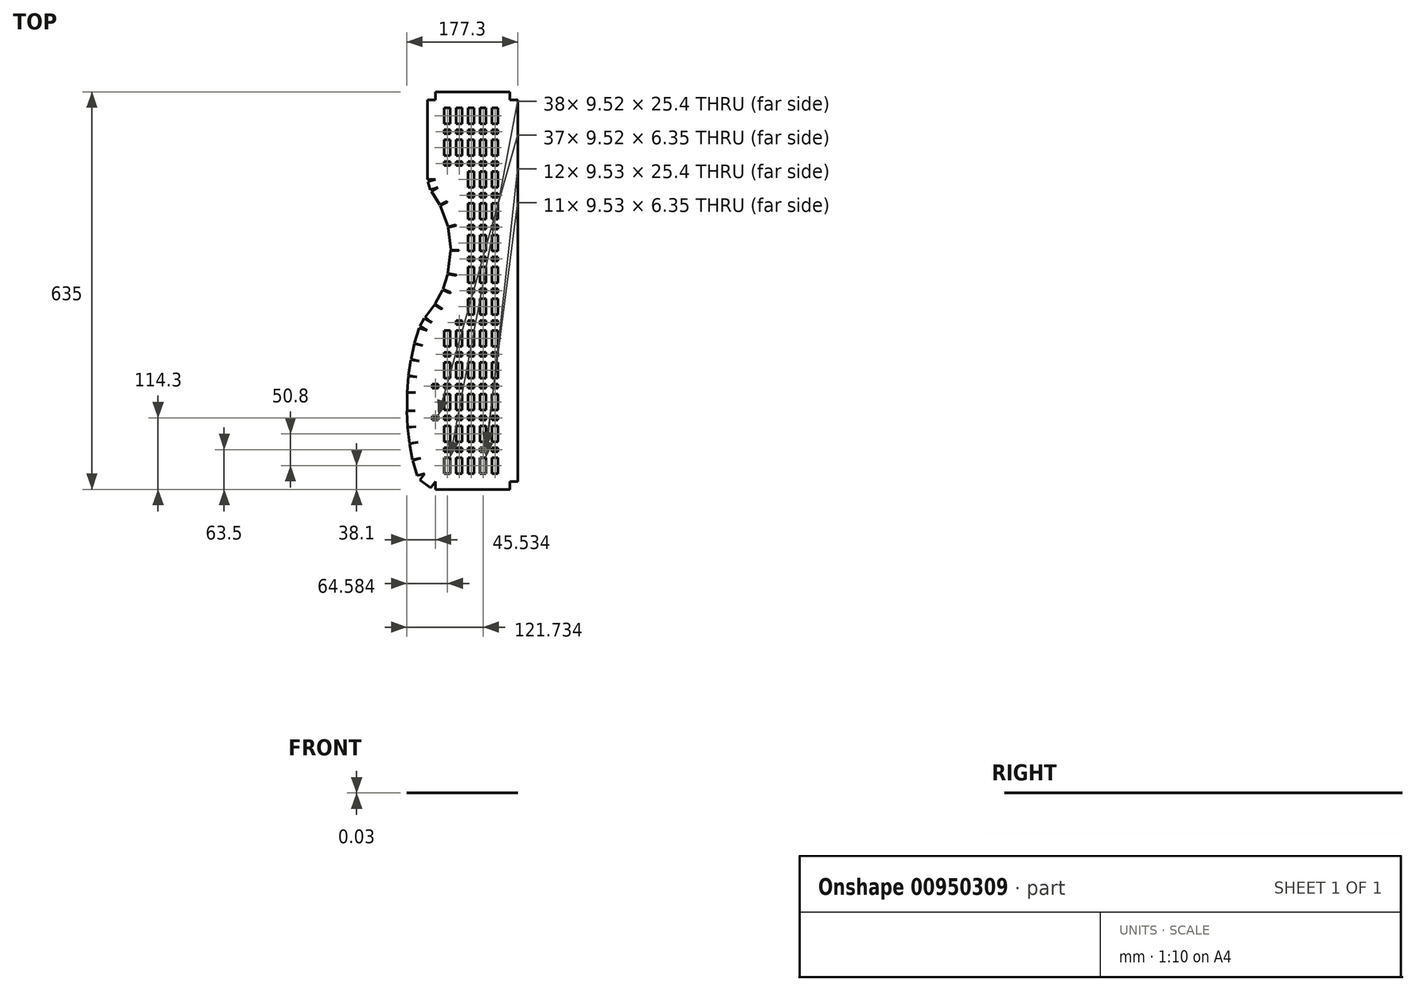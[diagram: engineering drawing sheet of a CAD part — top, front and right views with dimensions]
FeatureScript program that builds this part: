
annotation { "Feature Type Name" : "Feature", "Feature Type Description" : "" }
export const myFeature = defineFeature(function(context is Context, id is Id, definition is map)
    precondition{}
    {
        {
            var Q0;
            Q0=qCreatedBy(makeId("Top.planeOp"),FACE);
            var sketch = newSketch(context, id + "F0", { "sketchPlane" : qUnion([Q0])});
            skLineSegment(sketch, "E0", {"start": v(0, 0) * mm, "end": v(118.85, 0) * mm, "construction": true});
            skLineSegment(sketch, "E1", {"start": v(118.85, 0) * mm, "end": v(118.85, -609.6) * mm, "construction": true});
            skLineSegment(sketch, "E2", {"start": v(118.85, -609.6) * mm, "end": v(0, -609.6) * mm, "construction": true});
            skLineSegment(sketch, "E3", {"start": v(0, -622.3) * mm, "end": v(118.85, -622.3) * mm});
            skLineSegment(sketch, "E4", {"start": v(118.85, -622.3) * mm, "end": v(118.85, -609.6) * mm});
            skLineSegment(sketch, "E5", {"start": v(118.85, -609.6) * mm, "end": v(131.55, -609.6) * mm});
            skLineSegment(sketch, "E6", {"start": v(131.55, -609.6) * mm, "end": v(131.55, 0) * mm});
            skLineSegment(sketch, "E7", {"start": v(131.55, 0) * mm, "end": v(118.85, 0) * mm});
            skLineSegment(sketch, "E8", {"start": v(118.85, 0) * mm, "end": v(118.85, 12.7) * mm});
            skLineSegment(sketch, "E9", {"start": v(118.85, 12.7) * mm, "end": v(0, 12.7) * mm});
            skLineSegment(sketch, "E10", {"start": v(0, 12.7) * mm, "end": v(0, 0) * mm});
            skArc(sketch, "E11", {"start": v(0, -609.6) * mm, "mid": v(-10.58, -606.07) * mm, "end": v(-16.91, -596.9) * mm, "construction": true});
            skArc(sketch, "E12", {"start": v(-16.91, -596.9) * mm, "mid": v(-32.27, -482.32) * mm, "end": v(-13.22, -368.3) * mm, "construction": true});
            skLineSegment(sketch, "E13", {"start": v(-16.91, -596.9) * mm, "end": v(-13.22, -609.6) * mm, "construction": true});
            skPoint(sketch, "E14", {"position": v(-32.27, -482.32) * mm});
            skArc(sketch, "E15", {"start": v(-13.22, -368.3) * mm, "mid": v(-10.23, -361.57) * mm, "end": v(-5.93, -355.6) * mm, "construction": true});
            skArc(sketch, "E16", {"start": v(-5.93, -355.6) * mm, "mid": v(37.39, -249.44) * mm, "end": v(4.17, -139.7) * mm, "construction": true});
            skArc(sketch, "E17", {"start": v(4.17, -139.7) * mm, "mid": v(1.07, -133.68) * mm, "end": v(0, -127) * mm, "construction": true});
            skLineSegment(sketch, "E18", {"start": v(0, -127) * mm, "end": v(0, 0) * mm, "construction": true});
            skLineSegment(sketch, "E19", {"start": v(0, -609.6) * mm, "end": v(-7.63, -619.76) * mm});
            skLineSegment(sketch, "E20", {"start": v(-7.63, -619.76) * mm, "end": v(-24.54, -607.06) * mm});
            skLineSegment(sketch, "E21", {"start": v(-24.54, -607.06) * mm, "end": v(-16.91, -596.9) * mm});
            skLineSegment(sketch, "E22", {"start": v(0, -609.6) * mm, "end": v(0, -622.3) * mm});
            skLineSegment(sketch, "E23", {"start": v(-19.03, -599.72) * mm, "end": v(-2.12, -612.42) * mm, "construction": true});
            skPoint(sketch, "E24", {"position": v(-10.58, -606.07) * mm});
            skLineSegment(sketch, "E25", {"start": v(-10.58, -606.07) * mm, "end": v(-16.08, -613.4) * mm, "construction": true});
            skLineSegment(sketch, "E26", {"start": v(-16.91, -596.9) * mm, "end": v(-29.1, -600.44) * mm});
            skLineSegment(sketch, "E27", {"start": v(-29.1, -600.44) * mm, "end": v(-36.2, -576.05) * mm});
            skLineSegment(sketch, "E28", {"start": v(-36.2, -576.05) * mm, "end": v(-23.2, -572.28) * mm});
            skLineSegment(sketch, "E29", {"start": v(-23.2, -572.28) * mm, "end": v(-36.5, -574.76) * mm});
            skLineSegment(sketch, "E30", {"start": v(-36.5, -574.76) * mm, "end": v(-41.16, -549.79) * mm});
            skLineSegment(sketch, "E31", {"start": v(-41.16, -549.79) * mm, "end": v(-27.86, -547.3) * mm});
            skLineSegment(sketch, "E32", {"start": v(-27.86, -547.3) * mm, "end": v(-41.3, -548.91) * mm});
            skLineSegment(sketch, "E33", {"start": v(-41.3, -548.91) * mm, "end": v(-44.31, -523.7) * mm});
            skLineSegment(sketch, "E34", {"start": v(-44.31, -523.7) * mm, "end": v(-30.88, -522.09) * mm});
            skLineSegment(sketch, "E35", {"start": v(-30.88, -522.09) * mm, "end": v(-44.39, -522.81) * mm});
            skLineSegment(sketch, "E36", {"start": v(-44.39, -522.81) * mm, "end": v(-45.75, -497.45) * mm});
            skLineSegment(sketch, "E37", {"start": v(-45.75, -497.45) * mm, "end": v(-32.24, -496.72) * mm});
            skLineSegment(sketch, "E38", {"start": v(-32.24, -496.72) * mm, "end": v(-45.3, -496.72) * mm});
            skLineSegment(sketch, "E39", {"start": v(-45.3, -496.72) * mm, "end": v(-45.3, -467.92) * mm});
            skLineSegment(sketch, "E40", {"start": v(-45.3, -467.92) * mm, "end": v(-31.78, -467.92) * mm});
            skLineSegment(sketch, "E41", {"start": v(-32.27, -482.32) * mm, "end": v(-45.3, -482.32) * mm, "construction": true});
            skLineSegment(sketch, "E42", {"start": v(-31.78, -467.92) * mm, "end": v(-45.26, -466.76) * mm});
            skLineSegment(sketch, "E43", {"start": v(-45.26, -466.76) * mm, "end": v(-43.08, -441.45) * mm});
            skLineSegment(sketch, "E44", {"start": v(-43.08, -441.45) * mm, "end": v(-29.6, -442.61) * mm});
            skLineSegment(sketch, "E45", {"start": v(-33.51, -389.79) * mm, "end": v(-20.3, -392.7) * mm});
            skLineSegment(sketch, "E46", {"start": v(-20.3, -392.7) * mm, "end": v(-33.3, -388.93) * mm});
            skLineSegment(sketch, "E47", {"start": v(-33.3, -388.93) * mm, "end": v(-26.22, -364.53) * mm});
            skLineSegment(sketch, "E48", {"start": v(-26.22, -364.53) * mm, "end": v(-13.22, -368.3) * mm});
            skLineSegment(sketch, "E49", {"start": v(-38.98, -414.6) * mm, "end": v(-33.51, -389.79) * mm});
            skLineSegment(sketch, "E50", {"start": v(-38.98, -414.6) * mm, "end": v(-25.76, -417.5) * mm});
            skLineSegment(sketch, "E51", {"start": v(-25.76, -417.5) * mm, "end": v(-39.14, -415.46) * mm});
            skLineSegment(sketch, "E52", {"start": v(-39.14, -415.46) * mm, "end": v(-42.97, -440.57) * mm});
            skLineSegment(sketch, "E53", {"start": v(-42.97, -440.57) * mm, "end": v(-29.6, -442.61) * mm});
            skLineSegment(sketch, "E54", {"start": v(-23.2, -572.28) * mm, "end": v(-27.86, -547.3) * mm, "construction": true});
            skLineSegment(sketch, "E55", {"start": v(-27.86, -547.3) * mm, "end": v(-30.88, -522.09) * mm, "construction": true});
            skLineSegment(sketch, "E56", {"start": v(-30.88, -522.09) * mm, "end": v(-32.24, -496.72) * mm, "construction": true});
            skLineSegment(sketch, "E57", {"start": v(-31.78, -467.92) * mm, "end": v(-29.6, -442.61) * mm, "construction": true});
            skLineSegment(sketch, "E58", {"start": v(-29.6, -442.61) * mm, "end": v(-25.76, -417.5) * mm, "construction": true});
            skLineSegment(sketch, "E59", {"start": v(-25.76, -417.5) * mm, "end": v(-20.3, -392.7) * mm, "construction": true});
            skLineSegment(sketch, "E60", {"start": v(-20.3, -392.7) * mm, "end": v(-13.22, -368.3) * mm, "construction": true});
            skLineSegment(sketch, "E61", {"start": v(-13.22, -368.3) * mm, "end": v(-5.93, -355.6) * mm, "construction": true});
            skLineSegment(sketch, "E62", {"start": v(-5.93, -355.6) * mm, "end": v(-17.66, -348.86) * mm});
            skLineSegment(sketch, "E63", {"start": v(-17.66, -348.86) * mm, "end": v(-24.96, -361.56) * mm});
            skLineSegment(sketch, "E64", {"start": v(-24.96, -361.56) * mm, "end": v(-13.22, -368.3) * mm});
            skLineSegment(sketch, "E65", {"start": v(-5.93, -355.6) * mm, "end": v(-16.67, -347.37) * mm});
            skLineSegment(sketch, "E66", {"start": v(-16.67, -347.37) * mm, "end": v(-1.22, -327.2) * mm});
            skLineSegment(sketch, "E67", {"start": v(-1.22, -327.2) * mm, "end": v(9.52, -335.44) * mm, "construction": true});
            skLineSegment(sketch, "E68", {"start": v(9.52, -335.44) * mm, "end": v(-5.93, -355.6) * mm, "construction": true});
            skLineSegment(sketch, "E69", {"start": v(-0.53, -326.14) * mm, "end": v(11.44, -332.45) * mm, "construction": true});
            skLineSegment(sketch, "E70", {"start": v(11.44, -332.45) * mm, "end": v(23.28, -309.98) * mm, "construction": true});
            skLineSegment(sketch, "E71", {"start": v(23.28, -309.98) * mm, "end": v(11.31, -303.67) * mm, "construction": true});
            skLineSegment(sketch, "E72", {"start": v(11.31, -303.67) * mm, "end": v(-0.53, -326.14) * mm});
            skLineSegment(sketch, "E73", {"start": v(-0.53, -326.14) * mm, "end": v(10.83, -333.41) * mm});
            skLineSegment(sketch, "E74", {"start": v(-1.22, -327.2) * mm, "end": v(10.15, -334.48) * mm});
            skCircle(sketch, "E75", {"center": v(-0.53, -326.14) * mm, "radius": 1.27 * mm, "construction": true});
            skLineSegment(sketch, "E76", {"start": v(10.15, -334.48) * mm, "end": v(9.52, -335.44) * mm, "construction": true});
            skLineSegment(sketch, "E77", {"start": v(10.83, -333.41) * mm, "end": v(11.44, -332.45) * mm, "construction": true});
            skArc(sketch, "E78", {"start": v(10.15, -334.48) * mm, "mid": v(10.49, -333.95) * mm, "end": v(10.83, -333.41) * mm});
            skLineSegment(sketch, "E79", {"start": v(11.31, -303.67) * mm, "end": v(23.74, -308.93) * mm});
            skLineSegment(sketch, "E80", {"start": v(23.28, -309.98) * mm, "end": v(23.74, -308.93) * mm, "construction": true});
            skLineSegment(sketch, "E81", {"start": v(24.67, -306.7) * mm, "end": v(11.8, -302.5) * mm, "construction": true});
            skLineSegment(sketch, "E82", {"start": v(11.8, -302.5) * mm, "end": v(24.23, -307.76) * mm});
            skLineSegment(sketch, "E83", {"start": v(24.67, -306.7) * mm, "end": v(32.57, -282.57) * mm, "construction": true});
            skLineSegment(sketch, "E84", {"start": v(32.57, -282.57) * mm, "end": v(19.7, -278.36) * mm, "construction": true});
            skLineSegment(sketch, "E85", {"start": v(19.7, -278.36) * mm, "end": v(11.8, -302.5) * mm});
            skCircle(sketch, "E86", {"center": v(11.8, -302.5) * mm, "radius": 1.27 * mm, "construction": true});
            skLineSegment(sketch, "E87", {"start": v(24.67, -306.7) * mm, "end": v(24.23, -307.76) * mm, "construction": true});
            skArc(sketch, "E88", {"start": v(23.74, -308.93) * mm, "mid": v(23.99, -308.35) * mm, "end": v(24.23, -307.76) * mm});
            skLineSegment(sketch, "E89", {"start": v(19.7, -278.36) * mm, "end": v(32.9, -281.23) * mm});
            skLineSegment(sketch, "E90", {"start": v(37.57, -241.14) * mm, "end": v(24.13, -241.15) * mm});
            skLineSegment(sketch, "E91", {"start": v(24.13, -241.15) * mm, "end": v(37.57, -242.67) * mm, "construction": true});
            skLineSegment(sketch, "E92", {"start": v(20.04, -277.13) * mm, "end": v(33.18, -280) * mm});
            skLineSegment(sketch, "E93", {"start": v(20.04, -277.13) * mm, "end": v(33.49, -278.66) * mm, "construction": true});
            skLineSegment(sketch, "E94", {"start": v(33.49, -278.66) * mm, "end": v(37.57, -242.67) * mm, "construction": true});
            skLineSegment(sketch, "E95", {"start": v(24.13, -241.15) * mm, "end": v(20.04, -277.13) * mm});
            skCircle(sketch, "E96", {"center": v(20.04, -277.13) * mm, "radius": 1.27 * mm, "construction": true});
            skLineSegment(sketch, "E97", {"start": v(33.18, -280) * mm, "end": v(33.49, -278.66) * mm, "construction": true});
            skLineSegment(sketch, "E98", {"start": v(32.9, -281.23) * mm, "end": v(32.57, -282.57) * mm, "construction": true});
            skPoint(sketch, "E99", {"position": v(37.58, -241.42) * mm});
            skCircle(sketch, "E100", {"center": v(24.13, -241.15) * mm, "radius": 1.27 * mm, "construction": true});
            skLineSegment(sketch, "E101", {"start": v(37.57, -241.14) * mm, "end": v(37.57, -242.67) * mm, "construction": true});
            skArc(sketch, "E102", {"start": v(33.18, -280) * mm, "mid": v(33.04, -280.62) * mm, "end": v(32.9, -281.23) * mm});
            skLineSegment(sketch, "E103", {"start": v(0, 0) * mm, "end": v(-12.7, 0) * mm});
            skLineSegment(sketch, "E104", {"start": v(-12.7, 0) * mm, "end": v(-12.7, -127) * mm});
            skLineSegment(sketch, "E105", {"start": v(-12.7, -127) * mm, "end": v(0, -127) * mm});
            skLineSegment(sketch, "E106", {"start": v(0, -127) * mm, "end": v(4.17, -139.7) * mm, "construction": true});
            skLineSegment(sketch, "E107", {"start": v(4.17, -139.7) * mm, "end": v(-7.9, -143.66) * mm});
            skLineSegment(sketch, "E108", {"start": v(-7.9, -143.66) * mm, "end": v(-12.07, -130.96) * mm});
            skLineSegment(sketch, "E109", {"start": v(-12.07, -130.96) * mm, "end": v(0, -127) * mm});
            skLineSegment(sketch, "E110", {"start": v(4.17, -139.7) * mm, "end": v(-6.59, -146.45) * mm});
            skLineSegment(sketch, "E111", {"start": v(-6.59, -146.45) * mm, "end": v(6.92, -167.96) * mm});
            skLineSegment(sketch, "E112", {"start": v(6.92, -167.96) * mm, "end": v(17.67, -161.21) * mm, "construction": true});
            skLineSegment(sketch, "E113", {"start": v(17.67, -161.21) * mm, "end": v(4.17, -139.7) * mm, "construction": true});
            skLineSegment(sketch, "E114", {"start": v(6.92, -167.96) * mm, "end": v(18.27, -162.35) * mm});
            skLineSegment(sketch, "E115", {"start": v(18.27, -162.35) * mm, "end": v(17.67, -161.21) * mm, "construction": true});
            skLineSegment(sketch, "E116", {"start": v(7.53, -169.08) * mm, "end": v(18.85, -163.48) * mm});
            skLineSegment(sketch, "E117", {"start": v(18.85, -163.48) * mm, "end": v(19.43, -164.62) * mm, "construction": true});
            skLineSegment(sketch, "E118", {"start": v(19.43, -164.62) * mm, "end": v(7.53, -169.08) * mm, "construction": true});
            skLineSegment(sketch, "E119", {"start": v(7.53, -169.08) * mm, "end": v(20.24, -203) * mm});
            skLineSegment(sketch, "E120", {"start": v(20.24, -203) * mm, "end": v(32.13, -198.54) * mm, "construction": true});
            skLineSegment(sketch, "E121", {"start": v(32.13, -198.54) * mm, "end": v(19.43, -164.62) * mm, "construction": true});
            skCircle(sketch, "E122", {"center": v(6.92, -167.96) * mm, "radius": 1.27 * mm, "construction": true});
            skLineSegment(sketch, "E123", {"start": v(20.24, -203) * mm, "end": v(32.5, -200) * mm});
            skLineSegment(sketch, "E124", {"start": v(32.5, -200) * mm, "end": v(32.13, -198.54) * mm, "construction": true});
            skLineSegment(sketch, "E125", {"start": v(32.8, -201.22) * mm, "end": v(20.54, -204.23) * mm});
            skLineSegment(sketch, "E126", {"start": v(20.54, -204.23) * mm, "end": v(33.14, -202.68) * mm, "construction": true});
            skLineSegment(sketch, "E127", {"start": v(32.8, -201.22) * mm, "end": v(33.14, -202.68) * mm, "construction": true});
            skCircle(sketch, "E128", {"center": v(20.54, -204.23) * mm, "radius": 1.27 * mm, "construction": true});
            skLineSegment(sketch, "E129", {"start": v(24.95, -240.18) * mm, "end": v(37.57, -240.17) * mm});
            skLineSegment(sketch, "E130", {"start": v(20.54, -204.23) * mm, "end": v(24.95, -240.18) * mm});
            skLineSegment(sketch, "E131", {"start": v(24.95, -240.18) * mm, "end": v(37.55, -238.63) * mm, "construction": true});
            skLineSegment(sketch, "E132", {"start": v(37.55, -238.63) * mm, "end": v(37.57, -240.17) * mm, "construction": true});
            skLineSegment(sketch, "E133", {"start": v(37.55, -238.63) * mm, "end": v(33.14, -202.68) * mm, "construction": true});
            skArc(sketch, "E134", {"start": v(37.57, -241.14) * mm, "mid": v(37.57, -240.65) * mm, "end": v(37.57, -240.17) * mm});
            skArc(sketch, "E135", {"start": v(32.8, -201.22) * mm, "mid": v(32.65, -200.6) * mm, "end": v(32.5, -200) * mm});
            skArc(sketch, "E136", {"start": v(18.85, -163.48) * mm, "mid": v(18.56, -162.91) * mm, "end": v(18.27, -162.35) * mm});
            skLineSegment(sketch, "E137.0", {"start": v(12.7, -127) * mm, "end": v(12.7, -12.7) * mm, "construction": true});
            skArc(sketch, "E137.1", {"start": v(14.4, -132.17) * mm, "mid": v(13.14, -129.72) * mm, "end": v(12.7, -127) * mm, "construction": true});
            skLineSegment(sketch, "E137.2", {"start": v(12.7, -12.7) * mm, "end": v(106.15, -12.7) * mm, "construction": true});
            skArc(sketch, "E137.3", {"start": v(3.55, -364.05) * mm, "mid": v(50.07, -250.03) * mm, "end": v(14.4, -132.17) * mm, "construction": true});
            skArc(sketch, "E137.4", {"start": v(-1.15, -372.23) * mm, "mid": v(0.78, -367.9) * mm, "end": v(3.55, -364.05) * mm, "construction": true});
            skLineSegment(sketch, "E137.5", {"start": v(106.15, -12.7) * mm, "end": v(106.15, -596.9) * mm, "construction": true});
            skLineSegment(sketch, "E137.6", {"start": v(106.15, -596.9) * mm, "end": v(0, -596.9) * mm, "construction": true});
            skArc(sketch, "E137.7", {"start": v(0, -596.9) * mm, "mid": v(-2.95, -595.92) * mm, "end": v(-4.72, -593.36) * mm, "construction": true});
            skArc(sketch, "E137.8", {"start": v(-4.72, -593.36) * mm, "mid": v(-19.58, -482.53) * mm, "end": v(-1.15, -372.23) * mm, "construction": true});
            skSolve(sketch);
        }
        {
            var Q0;
            Q0=qSketchRegion(id+"F0",true);
            extrude(context, id + "F1", {"entities" : qUnion([Q0]), "depth" : 0.03 * mm, "offsetDistance" : 25.4 * mm});
        }
        {
            var Q0;
            Q0=qCreatedBy(makeId("Top.planeOp"),FACE);
            var sketch = newSketch(context, id + "F2", { "sketchPlane" : qUnion([Q0])});
            skLineSegment(sketch, "E138.bottom", {"start": v(99.8, -12.7) * mm, "end": v(90.27, -12.7) * mm});
            skLineSegment(sketch, "E138.top", {"start": v(99.8, -38.1) * mm, "end": v(90.27, -38.1) * mm});
            skLineSegment(sketch, "E138.left", {"start": v(99.8, -12.7) * mm, "end": v(99.8, -38.1) * mm});
            skLineSegment(sketch, "E138.right", {"start": v(90.27, -12.7) * mm, "end": v(90.27, -38.1) * mm});
            skLineSegment(sketch, "E139.bottom", {"start": v(90.27, -47.63) * mm, "end": v(99.8, -47.63) * mm});
            skLineSegment(sketch, "E139.top", {"start": v(90.27, -53.98) * mm, "end": v(99.8, -53.98) * mm});
            skLineSegment(sketch, "E139.left", {"start": v(90.27, -47.63) * mm, "end": v(90.27, -53.98) * mm});
            skLineSegment(sketch, "E139.right", {"start": v(99.8, -47.63) * mm, "end": v(99.8, -53.98) * mm});
            skLineSegment(sketch, "E140.0.1.0", {"start": v(90.27, -98.43) * mm, "end": v(99.8, -98.43) * mm});
            skLineSegment(sketch, "E140.0.1.1", {"start": v(99.8, -63.5) * mm, "end": v(90.27, -63.5) * mm});
            skLineSegment(sketch, "E140.0.1.2", {"start": v(99.8, -88.9) * mm, "end": v(90.27, -88.9) * mm});
            skLineSegment(sketch, "E140.0.1.3", {"start": v(90.27, -104.78) * mm, "end": v(99.8, -104.78) * mm});
            skLineSegment(sketch, "E140.0.1.4", {"start": v(90.27, -63.5) * mm, "end": v(90.27, -88.9) * mm});
            skLineSegment(sketch, "E140.0.1.5", {"start": v(99.8, -63.5) * mm, "end": v(99.8, -88.9) * mm});
            skLineSegment(sketch, "E140.0.1.6", {"start": v(99.8, -98.43) * mm, "end": v(99.8, -104.78) * mm});
            skLineSegment(sketch, "E140.0.1.7", {"start": v(90.27, -98.43) * mm, "end": v(90.27, -104.78) * mm});
            skLineSegment(sketch, "E140.0.2.0", {"start": v(90.27, -149.23) * mm, "end": v(99.8, -149.23) * mm});
            skLineSegment(sketch, "E140.0.2.1", {"start": v(99.8, -114.3) * mm, "end": v(90.27, -114.3) * mm});
            skLineSegment(sketch, "E140.0.2.2", {"start": v(99.8, -139.7) * mm, "end": v(90.27, -139.7) * mm});
            skLineSegment(sketch, "E140.0.2.3", {"start": v(90.27, -155.58) * mm, "end": v(99.8, -155.58) * mm});
            skLineSegment(sketch, "E140.0.2.4", {"start": v(90.27, -114.3) * mm, "end": v(90.27, -139.7) * mm});
            skLineSegment(sketch, "E140.0.2.5", {"start": v(99.8, -114.3) * mm, "end": v(99.8, -139.7) * mm});
            skLineSegment(sketch, "E140.0.2.6", {"start": v(99.8, -149.23) * mm, "end": v(99.8, -155.58) * mm});
            skLineSegment(sketch, "E140.0.2.7", {"start": v(90.27, -149.23) * mm, "end": v(90.27, -155.58) * mm});
            skLineSegment(sketch, "E140.0.3.0", {"start": v(90.27, -200.03) * mm, "end": v(99.8, -200.03) * mm});
            skLineSegment(sketch, "E140.0.3.1", {"start": v(99.8, -165.1) * mm, "end": v(90.27, -165.1) * mm});
            skLineSegment(sketch, "E140.0.3.2", {"start": v(99.8, -190.5) * mm, "end": v(90.27, -190.5) * mm});
            skLineSegment(sketch, "E140.0.3.3", {"start": v(90.27, -206.38) * mm, "end": v(99.8, -206.38) * mm});
            skLineSegment(sketch, "E140.0.3.4", {"start": v(90.27, -165.1) * mm, "end": v(90.27, -190.5) * mm});
            skLineSegment(sketch, "E140.0.3.5", {"start": v(99.8, -165.1) * mm, "end": v(99.8, -190.5) * mm});
            skLineSegment(sketch, "E140.0.3.6", {"start": v(99.8, -200.03) * mm, "end": v(99.8, -206.38) * mm});
            skLineSegment(sketch, "E140.0.3.7", {"start": v(90.27, -200.03) * mm, "end": v(90.27, -206.38) * mm});
            skLineSegment(sketch, "E140.0.4.0", {"start": v(90.27, -250.83) * mm, "end": v(99.8, -250.83) * mm});
            skLineSegment(sketch, "E140.0.4.1", {"start": v(99.8, -215.9) * mm, "end": v(90.27, -215.9) * mm});
            skLineSegment(sketch, "E140.0.4.2", {"start": v(99.8, -241.3) * mm, "end": v(90.27, -241.3) * mm});
            skLineSegment(sketch, "E140.0.4.3", {"start": v(90.27, -257.18) * mm, "end": v(99.8, -257.18) * mm});
            skLineSegment(sketch, "E140.0.4.4", {"start": v(90.27, -215.9) * mm, "end": v(90.27, -241.3) * mm});
            skLineSegment(sketch, "E140.0.4.5", {"start": v(99.8, -215.9) * mm, "end": v(99.8, -241.3) * mm});
            skLineSegment(sketch, "E140.0.4.6", {"start": v(99.8, -250.83) * mm, "end": v(99.8, -257.18) * mm});
            skLineSegment(sketch, "E140.0.4.7", {"start": v(90.27, -250.83) * mm, "end": v(90.27, -257.18) * mm});
            skLineSegment(sketch, "E140.0.5.0", {"start": v(90.27, -301.63) * mm, "end": v(99.8, -301.63) * mm});
            skLineSegment(sketch, "E140.0.5.1", {"start": v(99.8, -266.7) * mm, "end": v(90.27, -266.7) * mm});
            skLineSegment(sketch, "E140.0.5.2", {"start": v(99.8, -292.1) * mm, "end": v(90.27, -292.1) * mm});
            skLineSegment(sketch, "E140.0.5.3", {"start": v(90.27, -307.98) * mm, "end": v(99.8, -307.98) * mm});
            skLineSegment(sketch, "E140.0.5.4", {"start": v(90.27, -266.7) * mm, "end": v(90.27, -292.1) * mm});
            skLineSegment(sketch, "E140.0.5.5", {"start": v(99.8, -266.7) * mm, "end": v(99.8, -292.1) * mm});
            skLineSegment(sketch, "E140.0.5.6", {"start": v(99.8, -301.63) * mm, "end": v(99.8, -307.98) * mm});
            skLineSegment(sketch, "E140.0.5.7", {"start": v(90.27, -301.63) * mm, "end": v(90.27, -307.98) * mm});
            skLineSegment(sketch, "E140.0.6.0", {"start": v(90.27, -352.43) * mm, "end": v(99.8, -352.43) * mm});
            skLineSegment(sketch, "E140.0.6.1", {"start": v(99.8, -317.5) * mm, "end": v(90.27, -317.5) * mm});
            skLineSegment(sketch, "E140.0.6.2", {"start": v(99.8, -342.9) * mm, "end": v(90.27, -342.9) * mm});
            skLineSegment(sketch, "E140.0.6.3", {"start": v(90.27, -358.78) * mm, "end": v(99.8, -358.78) * mm});
            skLineSegment(sketch, "E140.0.6.4", {"start": v(90.27, -317.5) * mm, "end": v(90.27, -342.9) * mm});
            skLineSegment(sketch, "E140.0.6.5", {"start": v(99.8, -317.5) * mm, "end": v(99.8, -342.9) * mm});
            skLineSegment(sketch, "E140.0.6.6", {"start": v(99.8, -352.43) * mm, "end": v(99.8, -358.78) * mm});
            skLineSegment(sketch, "E140.0.6.7", {"start": v(90.27, -352.43) * mm, "end": v(90.27, -358.78) * mm});
            skLineSegment(sketch, "E140.0.7.0", {"start": v(90.27, -403.23) * mm, "end": v(99.8, -403.23) * mm});
            skLineSegment(sketch, "E140.0.7.1", {"start": v(99.8, -368.3) * mm, "end": v(90.27, -368.3) * mm});
            skLineSegment(sketch, "E140.0.7.2", {"start": v(99.8, -393.7) * mm, "end": v(90.27, -393.7) * mm});
            skLineSegment(sketch, "E140.0.7.3", {"start": v(90.27, -409.58) * mm, "end": v(99.8, -409.58) * mm});
            skLineSegment(sketch, "E140.0.7.4", {"start": v(90.27, -368.3) * mm, "end": v(90.27, -393.7) * mm});
            skLineSegment(sketch, "E140.0.7.5", {"start": v(99.8, -368.3) * mm, "end": v(99.8, -393.7) * mm});
            skLineSegment(sketch, "E140.0.7.6", {"start": v(99.8, -403.23) * mm, "end": v(99.8, -409.58) * mm});
            skLineSegment(sketch, "E140.0.7.7", {"start": v(90.27, -403.23) * mm, "end": v(90.27, -409.58) * mm});
            skLineSegment(sketch, "E140.0.8.0", {"start": v(90.27, -454.03) * mm, "end": v(99.8, -454.03) * mm});
            skLineSegment(sketch, "E140.0.8.1", {"start": v(99.8, -419.1) * mm, "end": v(90.27, -419.1) * mm});
            skLineSegment(sketch, "E140.0.8.2", {"start": v(99.8, -444.5) * mm, "end": v(90.27, -444.5) * mm});
            skLineSegment(sketch, "E140.0.8.3", {"start": v(90.27, -460.38) * mm, "end": v(99.8, -460.38) * mm});
            skLineSegment(sketch, "E140.0.8.4", {"start": v(90.27, -419.1) * mm, "end": v(90.27, -444.5) * mm});
            skLineSegment(sketch, "E140.0.8.5", {"start": v(99.8, -419.1) * mm, "end": v(99.8, -444.5) * mm});
            skLineSegment(sketch, "E140.0.8.6", {"start": v(99.8, -454.03) * mm, "end": v(99.8, -460.38) * mm});
            skLineSegment(sketch, "E140.0.8.7", {"start": v(90.27, -454.03) * mm, "end": v(90.27, -460.38) * mm});
            skLineSegment(sketch, "E140.0.9.0", {"start": v(90.27, -504.83) * mm, "end": v(99.8, -504.83) * mm});
            skLineSegment(sketch, "E140.0.9.1", {"start": v(99.8, -469.9) * mm, "end": v(90.27, -469.9) * mm});
            skLineSegment(sketch, "E140.0.9.2", {"start": v(99.8, -495.3) * mm, "end": v(90.27, -495.3) * mm});
            skLineSegment(sketch, "E140.0.9.3", {"start": v(90.27, -511.18) * mm, "end": v(99.8, -511.18) * mm});
            skLineSegment(sketch, "E140.0.9.4", {"start": v(90.27, -469.9) * mm, "end": v(90.27, -495.3) * mm});
            skLineSegment(sketch, "E140.0.9.5", {"start": v(99.8, -469.9) * mm, "end": v(99.8, -495.3) * mm});
            skLineSegment(sketch, "E140.0.9.6", {"start": v(99.8, -504.83) * mm, "end": v(99.8, -511.18) * mm});
            skLineSegment(sketch, "E140.0.9.7", {"start": v(90.27, -504.83) * mm, "end": v(90.27, -511.18) * mm});
            skLineSegment(sketch, "E140.0.10.0", {"start": v(90.27, -555.63) * mm, "end": v(99.8, -555.63) * mm});
            skLineSegment(sketch, "E140.0.10.1", {"start": v(99.8, -520.7) * mm, "end": v(90.27, -520.7) * mm});
            skLineSegment(sketch, "E140.0.10.2", {"start": v(99.8, -546.1) * mm, "end": v(90.27, -546.1) * mm});
            skLineSegment(sketch, "E140.0.10.3", {"start": v(90.27, -561.98) * mm, "end": v(99.8, -561.98) * mm});
            skLineSegment(sketch, "E140.0.10.4", {"start": v(90.27, -520.7) * mm, "end": v(90.27, -546.1) * mm});
            skLineSegment(sketch, "E140.0.10.5", {"start": v(99.8, -520.7) * mm, "end": v(99.8, -546.1) * mm});
            skLineSegment(sketch, "E140.0.10.6", {"start": v(99.8, -555.63) * mm, "end": v(99.8, -561.98) * mm});
            skLineSegment(sketch, "E140.0.10.7", {"start": v(90.27, -555.63) * mm, "end": v(90.27, -561.98) * mm});
            skLineSegment(sketch, "E140.0.11.1", {"start": v(99.8, -571.5) * mm, "end": v(90.27, -571.5) * mm});
            skLineSegment(sketch, "E140.0.11.2", {"start": v(99.8, -596.9) * mm, "end": v(90.27, -596.9) * mm});
            skLineSegment(sketch, "E140.0.11.4", {"start": v(90.27, -571.5) * mm, "end": v(90.27, -596.9) * mm});
            skLineSegment(sketch, "E140.0.11.5", {"start": v(99.8, -571.5) * mm, "end": v(99.8, -596.9) * mm});
            skLineSegment(sketch, "E140.1.0.0", {"start": v(71.22, -47.63) * mm, "end": v(80.75, -47.63) * mm});
            skLineSegment(sketch, "E140.1.0.1", {"start": v(80.75, -12.7) * mm, "end": v(71.22, -12.7) * mm});
            skLineSegment(sketch, "E140.1.0.2", {"start": v(80.75, -38.1) * mm, "end": v(71.22, -38.1) * mm});
            skLineSegment(sketch, "E140.1.0.3", {"start": v(71.22, -53.98) * mm, "end": v(80.75, -53.98) * mm});
            skLineSegment(sketch, "E140.1.0.4", {"start": v(71.22, -12.7) * mm, "end": v(71.22, -38.1) * mm});
            skLineSegment(sketch, "E140.1.0.5", {"start": v(80.75, -12.7) * mm, "end": v(80.75, -38.1) * mm});
            skLineSegment(sketch, "E140.1.0.6", {"start": v(80.75, -47.63) * mm, "end": v(80.75, -53.98) * mm});
            skLineSegment(sketch, "E140.1.0.7", {"start": v(71.22, -47.63) * mm, "end": v(71.22, -53.98) * mm});
            skLineSegment(sketch, "E140.1.1.0", {"start": v(71.22, -98.43) * mm, "end": v(80.75, -98.43) * mm});
            skLineSegment(sketch, "E140.1.1.1", {"start": v(80.75, -63.5) * mm, "end": v(71.22, -63.5) * mm});
            skLineSegment(sketch, "E140.1.1.2", {"start": v(80.75, -88.9) * mm, "end": v(71.22, -88.9) * mm});
            skLineSegment(sketch, "E140.1.1.3", {"start": v(71.22, -104.78) * mm, "end": v(80.75, -104.78) * mm});
            skLineSegment(sketch, "E140.1.1.4", {"start": v(71.22, -63.5) * mm, "end": v(71.22, -88.9) * mm});
            skLineSegment(sketch, "E140.1.1.5", {"start": v(80.75, -63.5) * mm, "end": v(80.75, -88.9) * mm});
            skLineSegment(sketch, "E140.1.1.6", {"start": v(80.75, -98.43) * mm, "end": v(80.75, -104.78) * mm});
            skLineSegment(sketch, "E140.1.1.7", {"start": v(71.22, -98.43) * mm, "end": v(71.22, -104.78) * mm});
            skLineSegment(sketch, "E140.1.2.0", {"start": v(71.22, -149.23) * mm, "end": v(80.75, -149.23) * mm});
            skLineSegment(sketch, "E140.1.2.1", {"start": v(80.75, -114.3) * mm, "end": v(71.22, -114.3) * mm});
            skLineSegment(sketch, "E140.1.2.2", {"start": v(80.75, -139.7) * mm, "end": v(71.22, -139.7) * mm});
            skLineSegment(sketch, "E140.1.2.3", {"start": v(71.22, -155.58) * mm, "end": v(80.75, -155.58) * mm});
            skLineSegment(sketch, "E140.1.2.4", {"start": v(71.22, -114.3) * mm, "end": v(71.22, -139.7) * mm});
            skLineSegment(sketch, "E140.1.2.5", {"start": v(80.75, -114.3) * mm, "end": v(80.75, -139.7) * mm});
            skLineSegment(sketch, "E140.1.2.6", {"start": v(80.75, -149.23) * mm, "end": v(80.75, -155.58) * mm});
            skLineSegment(sketch, "E140.1.2.7", {"start": v(71.22, -149.23) * mm, "end": v(71.22, -155.58) * mm});
            skLineSegment(sketch, "E140.1.3.0", {"start": v(71.22, -200.03) * mm, "end": v(80.75, -200.03) * mm});
            skLineSegment(sketch, "E140.1.3.1", {"start": v(80.75, -165.1) * mm, "end": v(71.22, -165.1) * mm});
            skLineSegment(sketch, "E140.1.3.2", {"start": v(80.75, -190.5) * mm, "end": v(71.22, -190.5) * mm});
            skLineSegment(sketch, "E140.1.3.3", {"start": v(71.22, -206.38) * mm, "end": v(80.75, -206.38) * mm});
            skLineSegment(sketch, "E140.1.3.4", {"start": v(71.22, -165.1) * mm, "end": v(71.22, -190.5) * mm});
            skLineSegment(sketch, "E140.1.3.5", {"start": v(80.75, -165.1) * mm, "end": v(80.75, -190.5) * mm});
            skLineSegment(sketch, "E140.1.3.6", {"start": v(80.75, -200.03) * mm, "end": v(80.75, -206.38) * mm});
            skLineSegment(sketch, "E140.1.3.7", {"start": v(71.22, -200.03) * mm, "end": v(71.22, -206.38) * mm});
            skLineSegment(sketch, "E140.1.4.0", {"start": v(71.22, -250.83) * mm, "end": v(80.75, -250.83) * mm});
            skLineSegment(sketch, "E140.1.4.1", {"start": v(80.75, -215.9) * mm, "end": v(71.22, -215.9) * mm});
            skLineSegment(sketch, "E140.1.4.2", {"start": v(80.75, -241.3) * mm, "end": v(71.22, -241.3) * mm});
            skLineSegment(sketch, "E140.1.4.3", {"start": v(71.22, -257.18) * mm, "end": v(80.75, -257.18) * mm});
            skLineSegment(sketch, "E140.1.4.4", {"start": v(71.22, -215.9) * mm, "end": v(71.22, -241.3) * mm});
            skLineSegment(sketch, "E140.1.4.5", {"start": v(80.75, -215.9) * mm, "end": v(80.75, -241.3) * mm});
            skLineSegment(sketch, "E140.1.4.6", {"start": v(80.75, -250.83) * mm, "end": v(80.75, -257.18) * mm});
            skLineSegment(sketch, "E140.1.4.7", {"start": v(71.22, -250.83) * mm, "end": v(71.22, -257.18) * mm});
            skLineSegment(sketch, "E140.1.5.0", {"start": v(71.22, -301.63) * mm, "end": v(80.75, -301.63) * mm});
            skLineSegment(sketch, "E140.1.5.1", {"start": v(80.75, -266.7) * mm, "end": v(71.22, -266.7) * mm});
            skLineSegment(sketch, "E140.1.5.2", {"start": v(80.75, -292.1) * mm, "end": v(71.22, -292.1) * mm});
            skLineSegment(sketch, "E140.1.5.3", {"start": v(71.22, -307.98) * mm, "end": v(80.75, -307.98) * mm});
            skLineSegment(sketch, "E140.1.5.4", {"start": v(71.22, -266.7) * mm, "end": v(71.22, -292.1) * mm});
            skLineSegment(sketch, "E140.1.5.5", {"start": v(80.75, -266.7) * mm, "end": v(80.75, -292.1) * mm});
            skLineSegment(sketch, "E140.1.5.6", {"start": v(80.75, -301.63) * mm, "end": v(80.75, -307.98) * mm});
            skLineSegment(sketch, "E140.1.5.7", {"start": v(71.22, -301.63) * mm, "end": v(71.22, -307.98) * mm});
            skLineSegment(sketch, "E140.1.6.0", {"start": v(71.22, -352.43) * mm, "end": v(80.75, -352.43) * mm});
            skLineSegment(sketch, "E140.1.6.1", {"start": v(80.75, -317.5) * mm, "end": v(71.22, -317.5) * mm});
            skLineSegment(sketch, "E140.1.6.2", {"start": v(80.75, -342.9) * mm, "end": v(71.22, -342.9) * mm});
            skLineSegment(sketch, "E140.1.6.3", {"start": v(71.22, -358.78) * mm, "end": v(80.75, -358.78) * mm});
            skLineSegment(sketch, "E140.1.6.4", {"start": v(71.22, -317.5) * mm, "end": v(71.22, -342.9) * mm});
            skLineSegment(sketch, "E140.1.6.5", {"start": v(80.75, -317.5) * mm, "end": v(80.75, -342.9) * mm});
            skLineSegment(sketch, "E140.1.6.6", {"start": v(80.75, -352.43) * mm, "end": v(80.75, -358.78) * mm});
            skLineSegment(sketch, "E140.1.6.7", {"start": v(71.22, -352.43) * mm, "end": v(71.22, -358.78) * mm});
            skLineSegment(sketch, "E140.1.7.0", {"start": v(71.22, -403.23) * mm, "end": v(80.75, -403.23) * mm});
            skLineSegment(sketch, "E140.1.7.1", {"start": v(80.75, -368.3) * mm, "end": v(71.22, -368.3) * mm});
            skLineSegment(sketch, "E140.1.7.2", {"start": v(80.75, -393.7) * mm, "end": v(71.22, -393.7) * mm});
            skLineSegment(sketch, "E140.1.7.3", {"start": v(71.22, -409.58) * mm, "end": v(80.75, -409.58) * mm});
            skLineSegment(sketch, "E140.1.7.4", {"start": v(71.22, -368.3) * mm, "end": v(71.22, -393.7) * mm});
            skLineSegment(sketch, "E140.1.7.5", {"start": v(80.75, -368.3) * mm, "end": v(80.75, -393.7) * mm});
            skLineSegment(sketch, "E140.1.7.6", {"start": v(80.75, -403.23) * mm, "end": v(80.75, -409.58) * mm});
            skLineSegment(sketch, "E140.1.7.7", {"start": v(71.22, -403.23) * mm, "end": v(71.22, -409.58) * mm});
            skLineSegment(sketch, "E140.1.8.0", {"start": v(71.22, -454.03) * mm, "end": v(80.75, -454.03) * mm});
            skLineSegment(sketch, "E140.1.8.1", {"start": v(80.75, -419.1) * mm, "end": v(71.22, -419.1) * mm});
            skLineSegment(sketch, "E140.1.8.2", {"start": v(80.75, -444.5) * mm, "end": v(71.22, -444.5) * mm});
            skLineSegment(sketch, "E140.1.8.3", {"start": v(71.22, -460.38) * mm, "end": v(80.75, -460.38) * mm});
            skLineSegment(sketch, "E140.1.8.4", {"start": v(71.22, -419.1) * mm, "end": v(71.22, -444.5) * mm});
            skLineSegment(sketch, "E140.1.8.5", {"start": v(80.75, -419.1) * mm, "end": v(80.75, -444.5) * mm});
            skLineSegment(sketch, "E140.1.8.6", {"start": v(80.75, -454.03) * mm, "end": v(80.75, -460.38) * mm});
            skLineSegment(sketch, "E140.1.8.7", {"start": v(71.22, -454.03) * mm, "end": v(71.22, -460.38) * mm});
            skLineSegment(sketch, "E140.1.9.0", {"start": v(71.22, -504.83) * mm, "end": v(80.75, -504.83) * mm});
            skLineSegment(sketch, "E140.1.9.1", {"start": v(80.75, -469.9) * mm, "end": v(71.22, -469.9) * mm});
            skLineSegment(sketch, "E140.1.9.2", {"start": v(80.75, -495.3) * mm, "end": v(71.22, -495.3) * mm});
            skLineSegment(sketch, "E140.1.9.3", {"start": v(71.22, -511.18) * mm, "end": v(80.75, -511.18) * mm});
            skLineSegment(sketch, "E140.1.9.4", {"start": v(71.22, -469.9) * mm, "end": v(71.22, -495.3) * mm});
            skLineSegment(sketch, "E140.1.9.5", {"start": v(80.75, -469.9) * mm, "end": v(80.75, -495.3) * mm});
            skLineSegment(sketch, "E140.1.9.6", {"start": v(80.75, -504.83) * mm, "end": v(80.75, -511.18) * mm});
            skLineSegment(sketch, "E140.1.9.7", {"start": v(71.22, -504.83) * mm, "end": v(71.22, -511.18) * mm});
            skLineSegment(sketch, "E140.1.10.0", {"start": v(71.22, -555.63) * mm, "end": v(80.75, -555.63) * mm});
            skLineSegment(sketch, "E140.1.10.1", {"start": v(80.75, -520.7) * mm, "end": v(71.22, -520.7) * mm});
            skLineSegment(sketch, "E140.1.10.2", {"start": v(80.75, -546.1) * mm, "end": v(71.22, -546.1) * mm});
            skLineSegment(sketch, "E140.1.10.3", {"start": v(71.22, -561.98) * mm, "end": v(80.75, -561.98) * mm});
            skLineSegment(sketch, "E140.1.10.4", {"start": v(71.22, -520.7) * mm, "end": v(71.22, -546.1) * mm});
            skLineSegment(sketch, "E140.1.10.5", {"start": v(80.75, -520.7) * mm, "end": v(80.75, -546.1) * mm});
            skLineSegment(sketch, "E140.1.10.6", {"start": v(80.75, -555.63) * mm, "end": v(80.75, -561.98) * mm});
            skLineSegment(sketch, "E140.1.10.7", {"start": v(71.22, -555.63) * mm, "end": v(71.22, -561.98) * mm});
            skLineSegment(sketch, "E140.1.11.1", {"start": v(80.75, -571.5) * mm, "end": v(71.22, -571.5) * mm});
            skLineSegment(sketch, "E140.1.11.2", {"start": v(80.75, -596.9) * mm, "end": v(71.22, -596.9) * mm});
            skLineSegment(sketch, "E140.1.11.4", {"start": v(71.22, -571.5) * mm, "end": v(71.22, -596.9) * mm});
            skLineSegment(sketch, "E140.1.11.5", {"start": v(80.75, -571.5) * mm, "end": v(80.75, -596.9) * mm});
            skLineSegment(sketch, "E140.2.0.0", {"start": v(52.17, -47.63) * mm, "end": v(61.7, -47.63) * mm});
            skLineSegment(sketch, "E140.2.0.1", {"start": v(61.7, -12.7) * mm, "end": v(52.17, -12.7) * mm});
            skLineSegment(sketch, "E140.2.0.2", {"start": v(61.7, -38.1) * mm, "end": v(52.17, -38.1) * mm});
            skLineSegment(sketch, "E140.2.0.3", {"start": v(52.17, -53.98) * mm, "end": v(61.7, -53.98) * mm});
            skLineSegment(sketch, "E140.2.0.4", {"start": v(52.17, -12.7) * mm, "end": v(52.17, -38.1) * mm});
            skLineSegment(sketch, "E140.2.0.5", {"start": v(61.7, -12.7) * mm, "end": v(61.7, -38.1) * mm});
            skLineSegment(sketch, "E140.2.0.6", {"start": v(61.7, -47.63) * mm, "end": v(61.7, -53.98) * mm});
            skLineSegment(sketch, "E140.2.0.7", {"start": v(52.17, -47.63) * mm, "end": v(52.17, -53.98) * mm});
            skLineSegment(sketch, "E140.2.1.0", {"start": v(52.17, -98.43) * mm, "end": v(61.7, -98.43) * mm});
            skLineSegment(sketch, "E140.2.1.1", {"start": v(61.7, -63.5) * mm, "end": v(52.17, -63.5) * mm});
            skLineSegment(sketch, "E140.2.1.2", {"start": v(61.7, -88.9) * mm, "end": v(52.17, -88.9) * mm});
            skLineSegment(sketch, "E140.2.1.3", {"start": v(52.17, -104.78) * mm, "end": v(61.7, -104.78) * mm});
            skLineSegment(sketch, "E140.2.1.4", {"start": v(52.17, -63.5) * mm, "end": v(52.17, -88.9) * mm});
            skLineSegment(sketch, "E140.2.1.5", {"start": v(61.7, -63.5) * mm, "end": v(61.7, -88.9) * mm});
            skLineSegment(sketch, "E140.2.1.6", {"start": v(61.7, -98.43) * mm, "end": v(61.7, -104.78) * mm});
            skLineSegment(sketch, "E140.2.1.7", {"start": v(52.17, -98.43) * mm, "end": v(52.17, -104.78) * mm});
            skLineSegment(sketch, "E140.2.2.0", {"start": v(52.17, -149.23) * mm, "end": v(61.7, -149.23) * mm});
            skLineSegment(sketch, "E140.2.2.1", {"start": v(61.7, -114.3) * mm, "end": v(52.17, -114.3) * mm});
            skLineSegment(sketch, "E140.2.2.2", {"start": v(61.7, -139.7) * mm, "end": v(52.17, -139.7) * mm});
            skLineSegment(sketch, "E140.2.2.3", {"start": v(52.17, -155.58) * mm, "end": v(61.7, -155.58) * mm});
            skLineSegment(sketch, "E140.2.2.4", {"start": v(52.17, -114.3) * mm, "end": v(52.17, -139.7) * mm});
            skLineSegment(sketch, "E140.2.2.5", {"start": v(61.7, -114.3) * mm, "end": v(61.7, -139.7) * mm});
            skLineSegment(sketch, "E140.2.2.6", {"start": v(61.7, -149.23) * mm, "end": v(61.7, -155.58) * mm});
            skLineSegment(sketch, "E140.2.2.7", {"start": v(52.17, -149.23) * mm, "end": v(52.17, -155.58) * mm});
            skLineSegment(sketch, "E140.2.3.0", {"start": v(52.17, -200.03) * mm, "end": v(61.7, -200.03) * mm});
            skLineSegment(sketch, "E140.2.3.1", {"start": v(61.7, -165.1) * mm, "end": v(52.17, -165.1) * mm});
            skLineSegment(sketch, "E140.2.3.2", {"start": v(61.7, -190.5) * mm, "end": v(52.17, -190.5) * mm});
            skLineSegment(sketch, "E140.2.3.3", {"start": v(52.17, -206.38) * mm, "end": v(61.7, -206.38) * mm});
            skLineSegment(sketch, "E140.2.3.4", {"start": v(52.17, -165.1) * mm, "end": v(52.17, -190.5) * mm});
            skLineSegment(sketch, "E140.2.3.5", {"start": v(61.7, -165.1) * mm, "end": v(61.7, -190.5) * mm});
            skLineSegment(sketch, "E140.2.3.6", {"start": v(61.7, -200.03) * mm, "end": v(61.7, -206.38) * mm});
            skLineSegment(sketch, "E140.2.3.7", {"start": v(52.17, -200.03) * mm, "end": v(52.17, -206.38) * mm});
            skLineSegment(sketch, "E140.2.4.0", {"start": v(52.17, -250.83) * mm, "end": v(61.7, -250.83) * mm});
            skLineSegment(sketch, "E140.2.4.1", {"start": v(61.7, -215.9) * mm, "end": v(52.17, -215.9) * mm});
            skLineSegment(sketch, "E140.2.4.2", {"start": v(61.7, -241.3) * mm, "end": v(52.17, -241.3) * mm});
            skLineSegment(sketch, "E140.2.4.3", {"start": v(52.17, -257.18) * mm, "end": v(61.7, -257.18) * mm});
            skLineSegment(sketch, "E140.2.4.4", {"start": v(52.17, -215.9) * mm, "end": v(52.17, -241.3) * mm});
            skLineSegment(sketch, "E140.2.4.5", {"start": v(61.7, -215.9) * mm, "end": v(61.7, -241.3) * mm});
            skLineSegment(sketch, "E140.2.4.6", {"start": v(61.7, -250.83) * mm, "end": v(61.7, -257.18) * mm});
            skLineSegment(sketch, "E140.2.4.7", {"start": v(52.17, -250.83) * mm, "end": v(52.17, -257.18) * mm});
            skLineSegment(sketch, "E140.2.5.0", {"start": v(52.17, -301.63) * mm, "end": v(61.7, -301.63) * mm});
            skLineSegment(sketch, "E140.2.5.1", {"start": v(61.7, -266.7) * mm, "end": v(52.17, -266.7) * mm});
            skLineSegment(sketch, "E140.2.5.2", {"start": v(61.7, -292.1) * mm, "end": v(52.17, -292.1) * mm});
            skLineSegment(sketch, "E140.2.5.3", {"start": v(52.17, -307.98) * mm, "end": v(61.7, -307.98) * mm});
            skLineSegment(sketch, "E140.2.5.4", {"start": v(52.17, -266.7) * mm, "end": v(52.17, -292.1) * mm});
            skLineSegment(sketch, "E140.2.5.5", {"start": v(61.7, -266.7) * mm, "end": v(61.7, -292.1) * mm});
            skLineSegment(sketch, "E140.2.5.6", {"start": v(61.7, -301.63) * mm, "end": v(61.7, -307.98) * mm});
            skLineSegment(sketch, "E140.2.5.7", {"start": v(52.17, -301.63) * mm, "end": v(52.17, -307.98) * mm});
            skLineSegment(sketch, "E140.2.6.0", {"start": v(52.17, -352.43) * mm, "end": v(61.7, -352.43) * mm});
            skLineSegment(sketch, "E140.2.6.1", {"start": v(61.7, -317.5) * mm, "end": v(52.17, -317.5) * mm});
            skLineSegment(sketch, "E140.2.6.2", {"start": v(61.7, -342.9) * mm, "end": v(52.17, -342.9) * mm});
            skLineSegment(sketch, "E140.2.6.3", {"start": v(52.17, -358.78) * mm, "end": v(61.7, -358.78) * mm});
            skLineSegment(sketch, "E140.2.6.4", {"start": v(52.17, -317.5) * mm, "end": v(52.17, -342.9) * mm});
            skLineSegment(sketch, "E140.2.6.5", {"start": v(61.7, -317.5) * mm, "end": v(61.7, -342.9) * mm});
            skLineSegment(sketch, "E140.2.6.6", {"start": v(61.7, -352.43) * mm, "end": v(61.7, -358.78) * mm});
            skLineSegment(sketch, "E140.2.6.7", {"start": v(52.17, -352.43) * mm, "end": v(52.17, -358.78) * mm});
            skLineSegment(sketch, "E140.2.7.0", {"start": v(52.17, -403.23) * mm, "end": v(61.7, -403.23) * mm});
            skLineSegment(sketch, "E140.2.7.1", {"start": v(61.7, -368.3) * mm, "end": v(52.17, -368.3) * mm});
            skLineSegment(sketch, "E140.2.7.2", {"start": v(61.7, -393.7) * mm, "end": v(52.17, -393.7) * mm});
            skLineSegment(sketch, "E140.2.7.3", {"start": v(52.17, -409.58) * mm, "end": v(61.7, -409.58) * mm});
            skLineSegment(sketch, "E140.2.7.4", {"start": v(52.17, -368.3) * mm, "end": v(52.17, -393.7) * mm});
            skLineSegment(sketch, "E140.2.7.5", {"start": v(61.7, -368.3) * mm, "end": v(61.7, -393.7) * mm});
            skLineSegment(sketch, "E140.2.7.6", {"start": v(61.7, -403.23) * mm, "end": v(61.7, -409.58) * mm});
            skLineSegment(sketch, "E140.2.7.7", {"start": v(52.17, -403.23) * mm, "end": v(52.17, -409.58) * mm});
            skLineSegment(sketch, "E140.2.8.0", {"start": v(52.17, -454.03) * mm, "end": v(61.7, -454.03) * mm});
            skLineSegment(sketch, "E140.2.8.1", {"start": v(61.7, -419.1) * mm, "end": v(52.17, -419.1) * mm});
            skLineSegment(sketch, "E140.2.8.2", {"start": v(61.7, -444.5) * mm, "end": v(52.17, -444.5) * mm});
            skLineSegment(sketch, "E140.2.8.3", {"start": v(52.17, -460.38) * mm, "end": v(61.7, -460.38) * mm});
            skLineSegment(sketch, "E140.2.8.4", {"start": v(52.17, -419.1) * mm, "end": v(52.17, -444.5) * mm});
            skLineSegment(sketch, "E140.2.8.5", {"start": v(61.7, -419.1) * mm, "end": v(61.7, -444.5) * mm});
            skLineSegment(sketch, "E140.2.8.6", {"start": v(61.7, -454.03) * mm, "end": v(61.7, -460.38) * mm});
            skLineSegment(sketch, "E140.2.8.7", {"start": v(52.17, -454.03) * mm, "end": v(52.17, -460.38) * mm});
            skLineSegment(sketch, "E140.2.9.0", {"start": v(52.17, -504.83) * mm, "end": v(61.7, -504.83) * mm});
            skLineSegment(sketch, "E140.2.9.1", {"start": v(61.7, -469.9) * mm, "end": v(52.17, -469.9) * mm});
            skLineSegment(sketch, "E140.2.9.2", {"start": v(61.7, -495.3) * mm, "end": v(52.17, -495.3) * mm});
            skLineSegment(sketch, "E140.2.9.3", {"start": v(52.17, -511.18) * mm, "end": v(61.7, -511.18) * mm});
            skLineSegment(sketch, "E140.2.9.4", {"start": v(52.17, -469.9) * mm, "end": v(52.17, -495.3) * mm});
            skLineSegment(sketch, "E140.2.9.5", {"start": v(61.7, -469.9) * mm, "end": v(61.7, -495.3) * mm});
            skLineSegment(sketch, "E140.2.9.6", {"start": v(61.7, -504.83) * mm, "end": v(61.7, -511.18) * mm});
            skLineSegment(sketch, "E140.2.9.7", {"start": v(52.17, -504.83) * mm, "end": v(52.17, -511.18) * mm});
            skLineSegment(sketch, "E140.2.10.0", {"start": v(52.17, -555.63) * mm, "end": v(61.7, -555.63) * mm});
            skLineSegment(sketch, "E140.2.10.1", {"start": v(61.7, -520.7) * mm, "end": v(52.17, -520.7) * mm});
            skLineSegment(sketch, "E140.2.10.2", {"start": v(61.7, -546.1) * mm, "end": v(52.17, -546.1) * mm});
            skLineSegment(sketch, "E140.2.10.3", {"start": v(52.17, -561.98) * mm, "end": v(61.7, -561.98) * mm});
            skLineSegment(sketch, "E140.2.10.4", {"start": v(52.17, -520.7) * mm, "end": v(52.17, -546.1) * mm});
            skLineSegment(sketch, "E140.2.10.5", {"start": v(61.7, -520.7) * mm, "end": v(61.7, -546.1) * mm});
            skLineSegment(sketch, "E140.2.10.6", {"start": v(61.7, -555.63) * mm, "end": v(61.7, -561.98) * mm});
            skLineSegment(sketch, "E140.2.10.7", {"start": v(52.17, -555.63) * mm, "end": v(52.17, -561.98) * mm});
            skLineSegment(sketch, "E140.2.11.1", {"start": v(61.7, -571.5) * mm, "end": v(52.17, -571.5) * mm});
            skLineSegment(sketch, "E140.2.11.2", {"start": v(61.7, -596.9) * mm, "end": v(52.17, -596.9) * mm});
            skLineSegment(sketch, "E140.2.11.4", {"start": v(52.17, -571.5) * mm, "end": v(52.17, -596.9) * mm});
            skLineSegment(sketch, "E140.2.11.5", {"start": v(61.7, -571.5) * mm, "end": v(61.7, -596.9) * mm});
            skLineSegment(sketch, "E140.3.0.0", {"start": v(33.12, -47.63) * mm, "end": v(42.65, -47.63) * mm});
            skLineSegment(sketch, "E140.3.0.1", {"start": v(42.65, -12.7) * mm, "end": v(33.12, -12.7) * mm});
            skLineSegment(sketch, "E140.3.0.2", {"start": v(42.65, -38.1) * mm, "end": v(33.12, -38.1) * mm});
            skLineSegment(sketch, "E140.3.0.3", {"start": v(33.12, -53.98) * mm, "end": v(42.65, -53.98) * mm});
            skLineSegment(sketch, "E140.3.0.4", {"start": v(33.12, -12.7) * mm, "end": v(33.12, -38.1) * mm});
            skLineSegment(sketch, "E140.3.0.5", {"start": v(42.65, -12.7) * mm, "end": v(42.65, -38.1) * mm});
            skLineSegment(sketch, "E140.3.0.6", {"start": v(42.65, -47.63) * mm, "end": v(42.65, -53.98) * mm});
            skLineSegment(sketch, "E140.3.0.7", {"start": v(33.12, -47.63) * mm, "end": v(33.12, -53.98) * mm});
            skLineSegment(sketch, "E140.3.1.0", {"start": v(33.12, -98.43) * mm, "end": v(42.65, -98.43) * mm});
            skLineSegment(sketch, "E140.3.1.1", {"start": v(42.65, -63.5) * mm, "end": v(33.12, -63.5) * mm});
            skLineSegment(sketch, "E140.3.1.2", {"start": v(42.65, -88.9) * mm, "end": v(33.12, -88.9) * mm});
            skLineSegment(sketch, "E140.3.1.3", {"start": v(33.12, -104.78) * mm, "end": v(42.65, -104.78) * mm});
            skLineSegment(sketch, "E140.3.1.4", {"start": v(33.12, -63.5) * mm, "end": v(33.12, -88.9) * mm});
            skLineSegment(sketch, "E140.3.1.5", {"start": v(42.65, -63.5) * mm, "end": v(42.65, -88.9) * mm});
            skLineSegment(sketch, "E140.3.1.6", {"start": v(42.65, -98.43) * mm, "end": v(42.65, -104.78) * mm});
            skLineSegment(sketch, "E140.3.1.7", {"start": v(33.12, -98.43) * mm, "end": v(33.12, -104.78) * mm});
            skLineSegment(sketch, "E140.3.6.0", {"start": v(33.12, -352.43) * mm, "end": v(42.65, -352.43) * mm});
            skLineSegment(sketch, "E140.3.6.3", {"start": v(33.12, -358.78) * mm, "end": v(42.65, -358.78) * mm});
            skLineSegment(sketch, "E140.3.6.6", {"start": v(42.65, -352.43) * mm, "end": v(42.65, -358.78) * mm});
            skLineSegment(sketch, "E140.3.6.7", {"start": v(33.12, -352.43) * mm, "end": v(33.12, -358.78) * mm});
            skLineSegment(sketch, "E140.3.7.0", {"start": v(33.12, -403.23) * mm, "end": v(42.65, -403.23) * mm});
            skLineSegment(sketch, "E140.3.7.1", {"start": v(42.65, -368.3) * mm, "end": v(33.12, -368.3) * mm});
            skLineSegment(sketch, "E140.3.7.2", {"start": v(42.65, -393.7) * mm, "end": v(33.12, -393.7) * mm});
            skLineSegment(sketch, "E140.3.7.3", {"start": v(33.12, -409.58) * mm, "end": v(42.65, -409.58) * mm});
            skLineSegment(sketch, "E140.3.7.4", {"start": v(33.12, -368.3) * mm, "end": v(33.12, -393.7) * mm});
            skLineSegment(sketch, "E140.3.7.5", {"start": v(42.65, -368.3) * mm, "end": v(42.65, -393.7) * mm});
            skLineSegment(sketch, "E140.3.7.6", {"start": v(42.65, -403.23) * mm, "end": v(42.65, -409.58) * mm});
            skLineSegment(sketch, "E140.3.7.7", {"start": v(33.12, -403.23) * mm, "end": v(33.12, -409.58) * mm});
            skLineSegment(sketch, "E140.3.8.0", {"start": v(33.12, -454.03) * mm, "end": v(42.65, -454.03) * mm});
            skLineSegment(sketch, "E140.3.8.1", {"start": v(42.65, -419.1) * mm, "end": v(33.12, -419.1) * mm});
            skLineSegment(sketch, "E140.3.8.2", {"start": v(42.65, -444.5) * mm, "end": v(33.12, -444.5) * mm});
            skLineSegment(sketch, "E140.3.8.3", {"start": v(33.12, -460.38) * mm, "end": v(42.65, -460.38) * mm});
            skLineSegment(sketch, "E140.3.8.4", {"start": v(33.12, -419.1) * mm, "end": v(33.12, -444.5) * mm});
            skLineSegment(sketch, "E140.3.8.5", {"start": v(42.65, -419.1) * mm, "end": v(42.65, -444.5) * mm});
            skLineSegment(sketch, "E140.3.8.6", {"start": v(42.65, -454.03) * mm, "end": v(42.65, -460.38) * mm});
            skLineSegment(sketch, "E140.3.8.7", {"start": v(33.12, -454.03) * mm, "end": v(33.12, -460.38) * mm});
            skLineSegment(sketch, "E140.3.9.0", {"start": v(33.12, -504.83) * mm, "end": v(42.65, -504.83) * mm});
            skLineSegment(sketch, "E140.3.9.1", {"start": v(42.65, -469.9) * mm, "end": v(33.12, -469.9) * mm});
            skLineSegment(sketch, "E140.3.9.2", {"start": v(42.65, -495.3) * mm, "end": v(33.12, -495.3) * mm});
            skLineSegment(sketch, "E140.3.9.3", {"start": v(33.12, -511.18) * mm, "end": v(42.65, -511.18) * mm});
            skLineSegment(sketch, "E140.3.9.4", {"start": v(33.12, -469.9) * mm, "end": v(33.12, -495.3) * mm});
            skLineSegment(sketch, "E140.3.9.5", {"start": v(42.65, -469.9) * mm, "end": v(42.65, -495.3) * mm});
            skLineSegment(sketch, "E140.3.9.6", {"start": v(42.65, -504.83) * mm, "end": v(42.65, -511.18) * mm});
            skLineSegment(sketch, "E140.3.9.7", {"start": v(33.12, -504.83) * mm, "end": v(33.12, -511.18) * mm});
            skLineSegment(sketch, "E140.3.10.0", {"start": v(33.12, -555.63) * mm, "end": v(42.65, -555.63) * mm});
            skLineSegment(sketch, "E140.3.10.1", {"start": v(42.65, -520.7) * mm, "end": v(33.12, -520.7) * mm});
            skLineSegment(sketch, "E140.3.10.2", {"start": v(42.65, -546.1) * mm, "end": v(33.12, -546.1) * mm});
            skLineSegment(sketch, "E140.3.10.3", {"start": v(33.12, -561.98) * mm, "end": v(42.65, -561.98) * mm});
            skLineSegment(sketch, "E140.3.10.4", {"start": v(33.12, -520.7) * mm, "end": v(33.12, -546.1) * mm});
            skLineSegment(sketch, "E140.3.10.5", {"start": v(42.65, -520.7) * mm, "end": v(42.65, -546.1) * mm});
            skLineSegment(sketch, "E140.3.10.6", {"start": v(42.65, -555.63) * mm, "end": v(42.65, -561.98) * mm});
            skLineSegment(sketch, "E140.3.10.7", {"start": v(33.12, -555.63) * mm, "end": v(33.12, -561.98) * mm});
            skLineSegment(sketch, "E140.3.11.1", {"start": v(42.65, -571.5) * mm, "end": v(33.12, -571.5) * mm});
            skLineSegment(sketch, "E140.3.11.2", {"start": v(42.65, -596.9) * mm, "end": v(33.12, -596.9) * mm});
            skLineSegment(sketch, "E140.3.11.4", {"start": v(33.12, -571.5) * mm, "end": v(33.12, -596.9) * mm});
            skLineSegment(sketch, "E140.3.11.5", {"start": v(42.65, -571.5) * mm, "end": v(42.65, -596.9) * mm});
            skLineSegment(sketch, "E140.4.0.0", {"start": v(14.07, -47.63) * mm, "end": v(23.6, -47.63) * mm});
            skLineSegment(sketch, "E140.4.0.1", {"start": v(23.6, -12.7) * mm, "end": v(14.07, -12.7) * mm});
            skLineSegment(sketch, "E140.4.0.2", {"start": v(23.6, -38.1) * mm, "end": v(14.07, -38.1) * mm});
            skLineSegment(sketch, "E140.4.0.3", {"start": v(14.07, -53.98) * mm, "end": v(23.6, -53.98) * mm});
            skLineSegment(sketch, "E140.4.0.4", {"start": v(14.07, -12.7) * mm, "end": v(14.07, -38.1) * mm});
            skLineSegment(sketch, "E140.4.0.5", {"start": v(23.6, -12.7) * mm, "end": v(23.6, -38.1) * mm});
            skLineSegment(sketch, "E140.4.0.6", {"start": v(23.6, -47.63) * mm, "end": v(23.6, -53.98) * mm});
            skLineSegment(sketch, "E140.4.0.7", {"start": v(14.07, -47.63) * mm, "end": v(14.07, -53.98) * mm});
            skLineSegment(sketch, "E140.4.1.0", {"start": v(14.07, -98.43) * mm, "end": v(23.6, -98.43) * mm});
            skLineSegment(sketch, "E140.4.1.1", {"start": v(23.6, -63.5) * mm, "end": v(14.07, -63.5) * mm});
            skLineSegment(sketch, "E140.4.1.2", {"start": v(23.6, -88.9) * mm, "end": v(14.07, -88.9) * mm});
            skLineSegment(sketch, "E140.4.1.3", {"start": v(14.07, -104.78) * mm, "end": v(23.6, -104.78) * mm});
            skLineSegment(sketch, "E140.4.1.4", {"start": v(14.07, -63.5) * mm, "end": v(14.07, -88.9) * mm});
            skLineSegment(sketch, "E140.4.1.5", {"start": v(23.6, -63.5) * mm, "end": v(23.6, -88.9) * mm});
            skLineSegment(sketch, "E140.4.1.6", {"start": v(23.6, -98.43) * mm, "end": v(23.6, -104.78) * mm});
            skLineSegment(sketch, "E140.4.1.7", {"start": v(14.07, -98.43) * mm, "end": v(14.07, -104.78) * mm});
            skLineSegment(sketch, "E140.4.7.0", {"start": v(14.07, -403.23) * mm, "end": v(23.6, -403.23) * mm});
            skLineSegment(sketch, "E140.4.7.1", {"start": v(23.6, -368.3) * mm, "end": v(14.07, -368.3) * mm});
            skLineSegment(sketch, "E140.4.7.2", {"start": v(23.6, -393.7) * mm, "end": v(14.07, -393.7) * mm});
            skLineSegment(sketch, "E140.4.7.3", {"start": v(14.07, -409.58) * mm, "end": v(23.6, -409.58) * mm});
            skLineSegment(sketch, "E140.4.7.4", {"start": v(14.07, -368.3) * mm, "end": v(14.07, -393.7) * mm});
            skLineSegment(sketch, "E140.4.7.5", {"start": v(23.6, -368.3) * mm, "end": v(23.6, -393.7) * mm});
            skLineSegment(sketch, "E140.4.7.6", {"start": v(23.6, -403.23) * mm, "end": v(23.6, -409.58) * mm});
            skLineSegment(sketch, "E140.4.7.7", {"start": v(14.07, -403.23) * mm, "end": v(14.07, -409.58) * mm});
            skLineSegment(sketch, "E140.4.8.0", {"start": v(14.07, -454.03) * mm, "end": v(23.6, -454.03) * mm});
            skLineSegment(sketch, "E140.4.8.1", {"start": v(23.6, -419.1) * mm, "end": v(14.07, -419.1) * mm});
            skLineSegment(sketch, "E140.4.8.2", {"start": v(23.6, -444.5) * mm, "end": v(14.07, -444.5) * mm});
            skLineSegment(sketch, "E140.4.8.3", {"start": v(14.07, -460.38) * mm, "end": v(23.6, -460.38) * mm});
            skLineSegment(sketch, "E140.4.8.4", {"start": v(14.07, -419.1) * mm, "end": v(14.07, -444.5) * mm});
            skLineSegment(sketch, "E140.4.8.5", {"start": v(23.6, -419.1) * mm, "end": v(23.6, -444.5) * mm});
            skLineSegment(sketch, "E140.4.8.6", {"start": v(23.6, -454.03) * mm, "end": v(23.6, -460.38) * mm});
            skLineSegment(sketch, "E140.4.8.7", {"start": v(14.07, -454.03) * mm, "end": v(14.07, -460.38) * mm});
            skLineSegment(sketch, "E140.4.9.0", {"start": v(14.07, -504.83) * mm, "end": v(23.6, -504.83) * mm});
            skLineSegment(sketch, "E140.4.9.1", {"start": v(23.6, -469.9) * mm, "end": v(14.07, -469.9) * mm});
            skLineSegment(sketch, "E140.4.9.2", {"start": v(23.6, -495.3) * mm, "end": v(14.07, -495.3) * mm});
            skLineSegment(sketch, "E140.4.9.3", {"start": v(14.07, -511.18) * mm, "end": v(23.6, -511.18) * mm});
            skLineSegment(sketch, "E140.4.9.4", {"start": v(14.07, -469.9) * mm, "end": v(14.07, -495.3) * mm});
            skLineSegment(sketch, "E140.4.9.5", {"start": v(23.6, -469.9) * mm, "end": v(23.6, -495.3) * mm});
            skLineSegment(sketch, "E140.4.9.6", {"start": v(23.6, -504.83) * mm, "end": v(23.6, -511.18) * mm});
            skLineSegment(sketch, "E140.4.9.7", {"start": v(14.07, -504.83) * mm, "end": v(14.07, -511.18) * mm});
            skLineSegment(sketch, "E140.4.10.0", {"start": v(14.07, -555.63) * mm, "end": v(23.6, -555.63) * mm});
            skLineSegment(sketch, "E140.4.10.1", {"start": v(23.6, -520.7) * mm, "end": v(14.07, -520.7) * mm});
            skLineSegment(sketch, "E140.4.10.2", {"start": v(23.6, -546.1) * mm, "end": v(14.07, -546.1) * mm});
            skLineSegment(sketch, "E140.4.10.3", {"start": v(14.07, -561.98) * mm, "end": v(23.6, -561.98) * mm});
            skLineSegment(sketch, "E140.4.10.4", {"start": v(14.07, -520.7) * mm, "end": v(14.07, -546.1) * mm});
            skLineSegment(sketch, "E140.4.10.5", {"start": v(23.6, -520.7) * mm, "end": v(23.6, -546.1) * mm});
            skLineSegment(sketch, "E140.4.10.6", {"start": v(23.6, -555.63) * mm, "end": v(23.6, -561.98) * mm});
            skLineSegment(sketch, "E140.4.10.7", {"start": v(14.07, -555.63) * mm, "end": v(14.07, -561.98) * mm});
            skLineSegment(sketch, "E140.4.11.1", {"start": v(23.6, -571.5) * mm, "end": v(14.07, -571.5) * mm});
            skLineSegment(sketch, "E140.4.11.2", {"start": v(23.6, -596.9) * mm, "end": v(14.07, -596.9) * mm});
            skLineSegment(sketch, "E140.4.11.4", {"start": v(14.07, -571.5) * mm, "end": v(14.07, -596.9) * mm});
            skLineSegment(sketch, "E140.4.11.5", {"start": v(23.6, -571.5) * mm, "end": v(23.6, -596.9) * mm});
            skLineSegment(sketch, "E140.5.8.0", {"start": v(-4.98, -454.03) * mm, "end": v(4.55, -454.03) * mm});
            skLineSegment(sketch, "E140.5.8.3", {"start": v(-4.98, -460.38) * mm, "end": v(4.55, -460.38) * mm});
            skLineSegment(sketch, "E140.5.8.6", {"start": v(4.55, -454.03) * mm, "end": v(4.55, -460.38) * mm});
            skLineSegment(sketch, "E140.5.8.7", {"start": v(-4.98, -454.03) * mm, "end": v(-4.98, -460.38) * mm});
            skLineSegment(sketch, "E140.5.9.0", {"start": v(-4.98, -504.83) * mm, "end": v(4.55, -504.83) * mm});
            skLineSegment(sketch, "E140.5.9.3", {"start": v(-4.98, -511.18) * mm, "end": v(4.55, -511.18) * mm});
            skLineSegment(sketch, "E140.5.9.6", {"start": v(4.55, -504.83) * mm, "end": v(4.55, -511.18) * mm});
            skLineSegment(sketch, "E140.5.9.7", {"start": v(-4.98, -504.83) * mm, "end": v(-4.98, -511.18) * mm});
            skLineSegment(sketch, "E140.direction1", {"start": v(90.27, -53.98) * mm, "end": v(71.22, -53.98) * mm, "construction": true});
            skLineSegment(sketch, "E140.direction2", {"start": v(90.27, -53.98) * mm, "end": v(90.27, -104.78) * mm, "construction": true});
            skSolve(sketch);
        }
        {
            var Q0;
            Q0=qSketchRegion(id+"F2",true);
            extrude(context, id + "F3", {"entities" : qUnion([Q0]), "operationType" : NewBodyOperationType.REMOVE, "endBound" : BoundingType.THROUGH_ALL, "depth" : 25.4 * mm, "offsetDistance" : 25.4 * mm});
        }
    });
